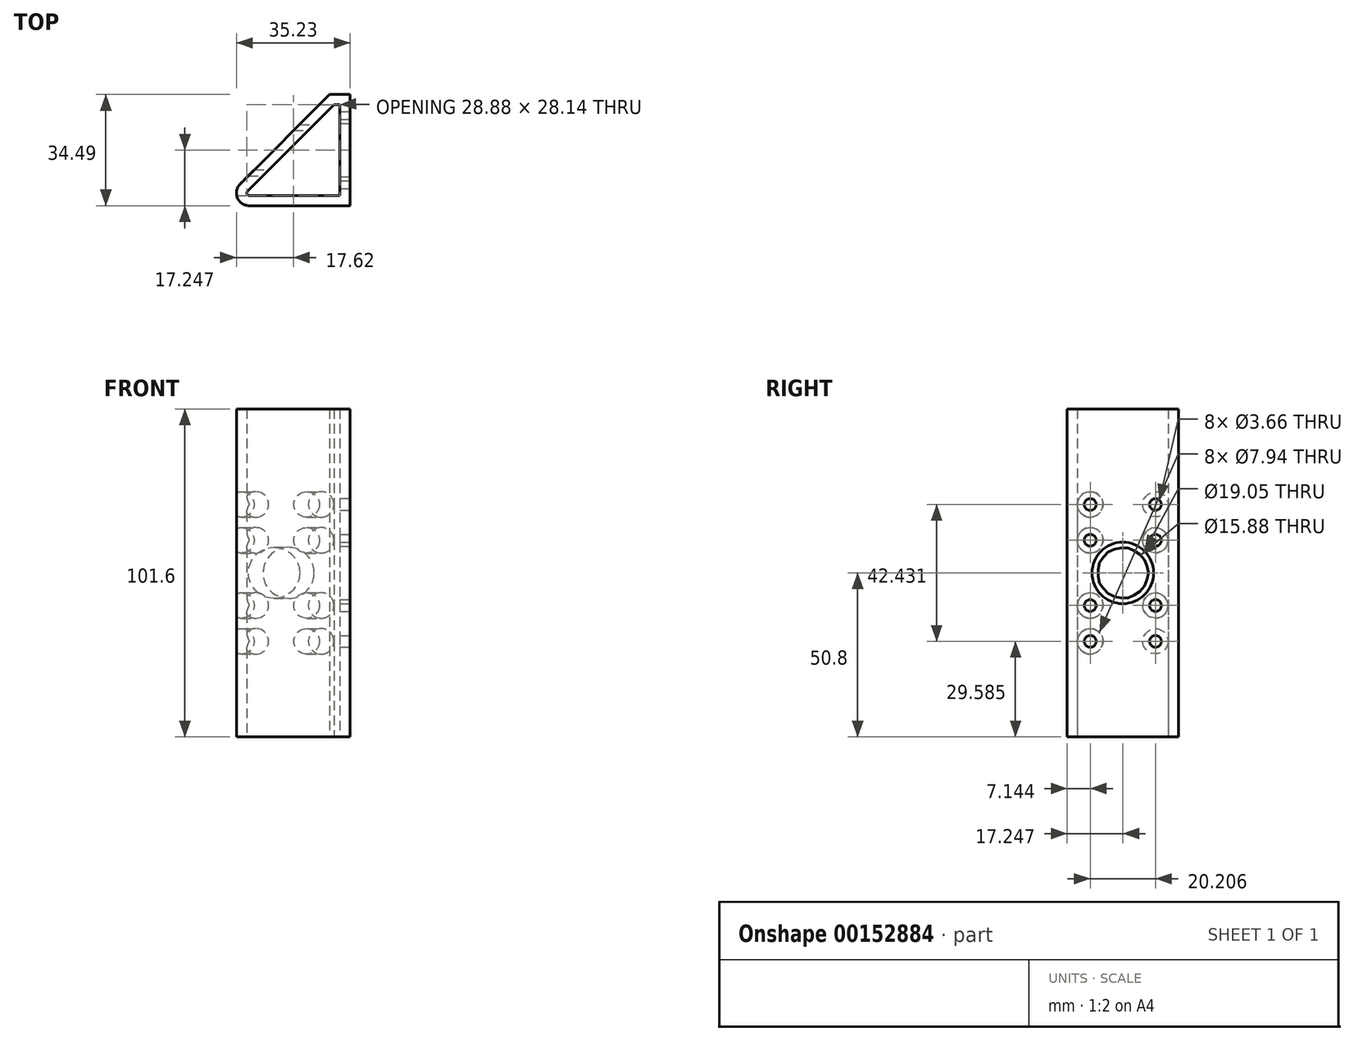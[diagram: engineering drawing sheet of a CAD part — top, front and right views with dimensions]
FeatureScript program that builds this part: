
annotation { "Feature Type Name" : "Feature", "Feature Type Description" : "" }
export const myFeature = defineFeature(function(context is Context, id is Id, definition is map)
    precondition{}
    {
        {
            var Q0;
            Q0=qCreatedBy(makeId("Top.planeOp"),FACE);
            var sketch = newSketch(context, id + "F0", { "sketchPlane" : qUnion([Q0])});
            skLineSegment(sketch, "E0", {"start": v(0.56, -1.36) * mm, "end": v(28.65, -1.36) * mm});
            skLineSegment(sketch, "E1", {"start": v(26.79, 26.79) * mm, "end": v(0, 0) * mm});
            skArc(sketch, "E2", {"start": v(-2.25, 2.25) * mm, "mid": v(-3.1, -2.08) * mm, "end": v(0.56, -4.53) * mm});
            skLineSegment(sketch, "E3", {"start": v(-2.25, 2.25) * mm, "end": v(25.47, 29.96) * mm});
            skLineSegment(sketch, "E4", {"start": v(0.56, -4.53) * mm, "end": v(31.82, -4.53) * mm});
            skLineSegment(sketch, "E5", {"start": v(31.82, -4.53) * mm, "end": v(31.82, 29.96) * mm});
            skLineSegment(sketch, "E6", {"start": v(28.65, -1.36) * mm, "end": v(28.65, -4.53) * mm, "construction": true});
            skLineSegment(sketch, "E7", {"start": v(28.65, -1.36) * mm, "end": v(31.82, -1.36) * mm, "construction": true});
            skArc(sketch, "E8", {"start": v(0, 0) * mm, "mid": v(-0.17, -0.87) * mm, "end": v(0.56, -1.36) * mm});
            skLineSegment(sketch, "E9", {"start": v(25.47, 29.96) * mm, "end": v(31.82, 29.96) * mm});
            skLineSegment(sketch, "E10", {"start": v(26.79, 26.79) * mm, "end": v(28.65, 26.79) * mm});
            skLineSegment(sketch, "E11", {"start": v(28.65, -1.36) * mm, "end": v(28.65, 26.79) * mm});
            skLineSegment(sketch, "E12", {"start": v(28.65, 26.79) * mm, "end": v(28.65, 29.96) * mm, "construction": true});
            skSolve(sketch);
        }
        {
            var Q0;
            Q0 = qSketchRegion(id + "F0", true);
            extrude(context, id + "F1", {"entities" : qUnion([Q0]), "depth" : 101.6 * mm});
        }
        {
            var Q0;
            Q0=makeQuery(id+"F1.opExtrude","SWEPT_FACE",FACE,{"disambiguationData":[OSD([sQuery(id+"F0.wireOp",EDGE,"E5")])]});
            var sketch = newSketch(context, id + "F2", { "sketchPlane" : qUnion([Q0])});
            skLineSegment(sketch, "E13", {"start": v(26.79, 50.8) * mm, "end": v(-1.36, 50.8) * mm, "construction": true});
            skLineSegment(sketch, "E14.bottom", {"start": v(-1.36, 0) * mm, "end": v(2.61, 0) * mm, "construction": true});
            skLineSegment(sketch, "E14.top", {"start": v(-1.36, 29.58) * mm, "end": v(2.61, 29.58) * mm, "construction": true});
            skLineSegment(sketch, "E14.left", {"start": v(-1.36, 0) * mm, "end": v(-1.36, 29.58) * mm, "construction": true});
            skLineSegment(sketch, "E14.right", {"start": v(2.61, 0) * mm, "end": v(2.61, 29.58) * mm, "construction": true});
            skLineSegment(sketch, "E15.bottom", {"start": v(2.61, 29.58) * mm, "end": v(22.82, 29.58) * mm, "construction": true});
            skLineSegment(sketch, "E15.top", {"start": v(2.61, 72.02) * mm, "end": v(22.82, 72.02) * mm, "construction": true});
            skLineSegment(sketch, "E15.left", {"start": v(2.61, 29.58) * mm, "end": v(2.61, 72.02) * mm, "construction": true});
            skLineSegment(sketch, "E15.right", {"start": v(22.82, 29.58) * mm, "end": v(22.82, 72.02) * mm, "construction": true});
            skPoint(sketch, "E15.middle", {"position": v(12.72, 50.8) * mm});
            skCircle(sketch, "E16", {"center": v(2.61, 29.58) * mm, "radius": 1.83 * mm});
            skCircle(sketch, "E17", {"center": v(22.82, 29.58) * mm, "radius": 1.83 * mm});
            skCircle(sketch, "E18", {"center": v(22.82, 72.02) * mm, "radius": 1.83 * mm});
            skCircle(sketch, "E19", {"center": v(2.61, 72.02) * mm, "radius": 1.83 * mm});
            skCircle(sketch, "E20", {"center": v(12.72, 50.8) * mm, "radius": 9.53 * mm});
            skLineSegment(sketch, "E21.bottom", {"start": v(22.82, 40.7) * mm, "end": v(2.61, 40.7) * mm, "construction": true});
            skLineSegment(sketch, "E21.top", {"start": v(22.82, 60.9) * mm, "end": v(2.61, 60.9) * mm, "construction": true});
            skLineSegment(sketch, "E21.left", {"start": v(22.82, 40.7) * mm, "end": v(22.82, 60.9) * mm, "construction": true});
            skLineSegment(sketch, "E21.right", {"start": v(2.61, 40.7) * mm, "end": v(2.61, 60.9) * mm, "construction": true});
            skCircle(sketch, "E22", {"center": v(22.82, 40.7) * mm, "radius": 3.17 * mm, "construction": true});
            skCircle(sketch, "E23", {"center": v(12.72, 50.8) * mm, "radius": 11.11 * mm, "construction": true});
            skCircle(sketch, "E24", {"center": v(22.82, 60.9) * mm, "radius": 1.83 * mm});
            skCircle(sketch, "E25", {"center": v(22.82, 40.7) * mm, "radius": 1.83 * mm});
            skCircle(sketch, "E26", {"center": v(2.61, 40.7) * mm, "radius": 1.83 * mm});
            skCircle(sketch, "E27", {"center": v(2.61, 60.9) * mm, "radius": 1.83 * mm});
            skSolve(sketch);
        }
        {
            var Q0;
            Q0 = qSketchRegion(id + "F2", true);
            var Q1;
            Q1=makeQuery(id+"F1.opExtrude","SWEPT_FACE",FACE,{"disambiguationData":[OSD([sQuery(id+"F0.wireOp",EDGE,"E11")])]});
            extrude(context, id + "F3", {"entities" : qUnion([Q0]), "operationType" : NewBodyOperationType.REMOVE, "endBound" : BoundingType.UP_TO_SURFACE, "oppositeDirection" : true, "endBoundEntityFace" : qUnion([Q1]), "depth" : 25.4 * mm});
        }
        {
            var Q0;
            Q0=makeQuery(id+"F1.opExtrude","SWEPT_FACE",FACE,{"disambiguationData":[OSD([sQuery(id+"F0.wireOp",EDGE,"E11")])]});
            var sketch = newSketch(context, id + "F4", { "sketchPlane" : qUnion([Q0])});
            skCircle(sketch, "E28", {"center": v(-22.82, 29.58) * mm, "radius": 3.97 * mm});
            skCircle(sketch, "E29", {"center": v(-2.61, 29.58) * mm, "radius": 3.97 * mm});
            skCircle(sketch, "E30", {"center": v(-2.61, 72.02) * mm, "radius": 3.97 * mm});
            skCircle(sketch, "E31", {"center": v(-22.82, 72.02) * mm, "radius": 3.97 * mm});
            skCircle(sketch, "E32", {"center": v(-2.61, 40.7) * mm, "radius": 3.97 * mm});
            skCircle(sketch, "E33", {"center": v(-2.61, 60.9) * mm, "radius": 3.97 * mm});
            skCircle(sketch, "E34", {"center": v(-22.82, 40.7) * mm, "radius": 3.97 * mm});
            skCircle(sketch, "E35", {"center": v(-22.82, 60.9) * mm, "radius": 3.97 * mm});
            skCircle(sketch, "E36", {"center": v(-12.72, 50.8) * mm, "radius": 7.94 * mm});
            skSolve(sketch);
        }
        {
            var Q0;
            Q0 = qSketchRegion(id + "F4", true);
            var Q1;
            Q1=makeQuery(id+"F1.opExtrude","SWEPT_FACE",FACE,{"disambiguationData":[OSD([sQuery(id+"F0.wireOp",EDGE,"E3")])]});
            extrude(context, id + "F5", {"entities" : qUnion([Q0]), "operationType" : NewBodyOperationType.REMOVE, "endBound" : BoundingType.UP_TO_SURFACE, "endBoundEntityFace" : qUnion([Q1]), "depth" : 25.4 * mm});
        }
    });
